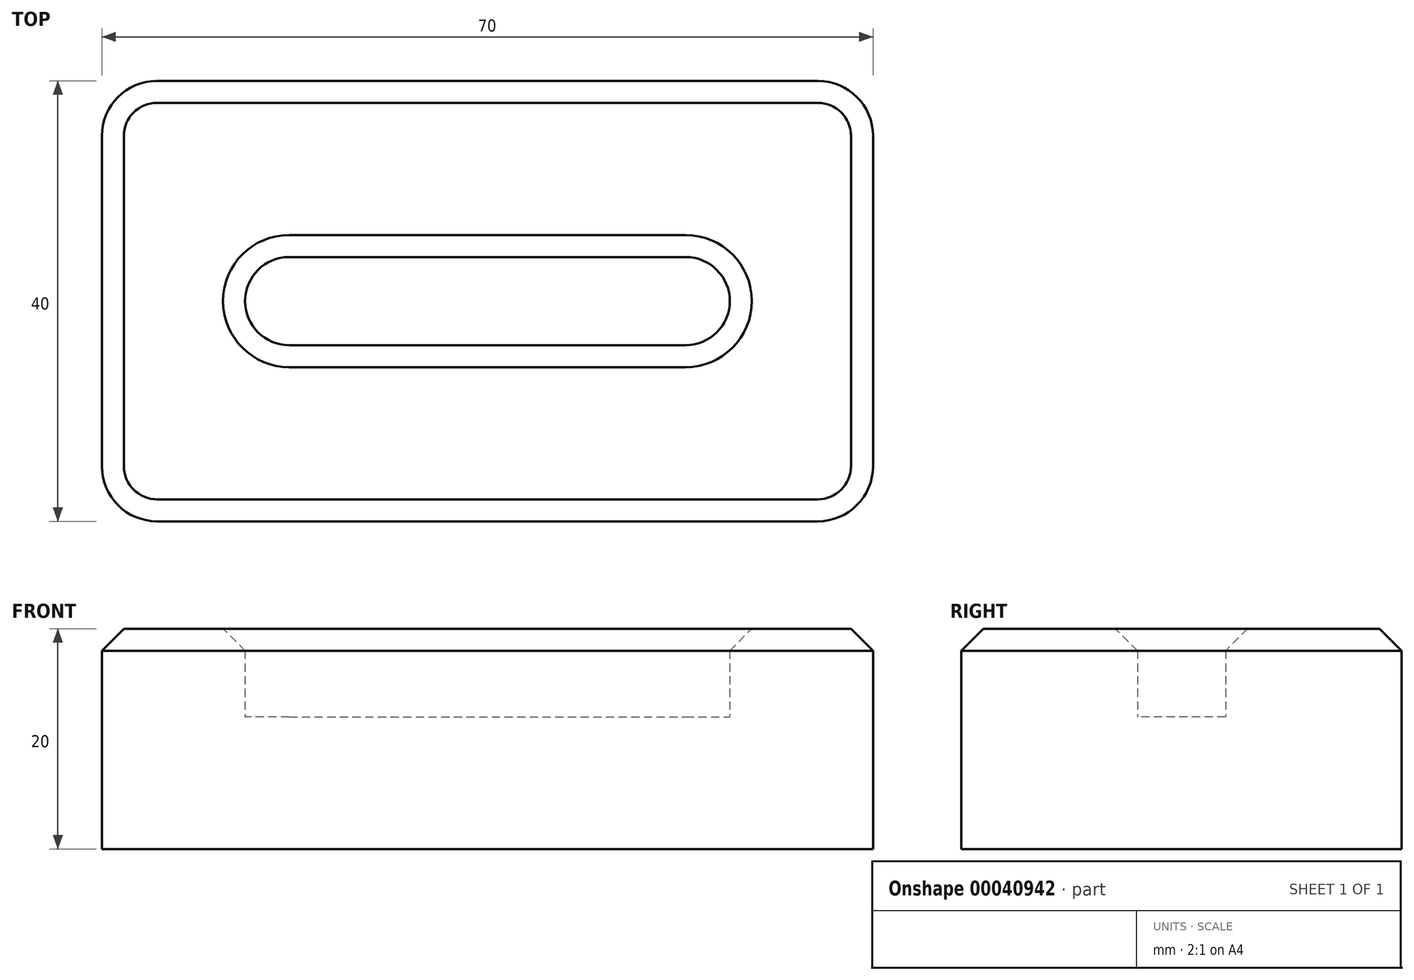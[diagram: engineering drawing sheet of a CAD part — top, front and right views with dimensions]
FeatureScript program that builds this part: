
annotation { "Feature Type Name" : "Feature", "Feature Type Description" : "" }
export const myFeature = defineFeature(function(context is Context, id is Id, definition is map)
    precondition{}
    {
        {
            var Q0;
            Q0=qCreatedBy(makeId("Top.planeOp"),FACE);
            var sketch = newSketch(context, id + "F0", { "sketchPlane" : qUnion([Q0])});
            skLineSegment(sketch, "E0.bottom", {"start": v(-5, 0) * mm, "end": v(-65, 0) * mm});
            skLineSegment(sketch, "E0.top", {"start": v(-5, 40) * mm, "end": v(-65, 40) * mm});
            skLineSegment(sketch, "E0.left", {"start": v(0, 5) * mm, "end": v(0, 35) * mm});
            skLineSegment(sketch, "E0.right", {"start": v(-70, 5) * mm, "end": v(-70, 35) * mm});
            skLineSegment(sketch, "E1.bottom", {"start": v(-53, 24) * mm, "end": v(-17, 24) * mm});
            skLineSegment(sketch, "E1.top", {"start": v(-53, 16) * mm, "end": v(-17, 16) * mm});
            skLineSegment(sketch, "E1.left", {"start": v(-57, 20) * mm, "end": v(-57, 20) * mm});
            skLineSegment(sketch, "E1.right", {"start": v(-13, 20) * mm, "end": v(-13, 20) * mm});
            skPoint(sketch, "E2.visualSharp", {"position": v(-57, 24) * mm});
            skArc(sketch, "E2.filletArc", {"start": v(-53, 24) * mm, "mid": v(-55.83, 22.83) * mm, "end": v(-57, 20) * mm});
            skPoint(sketch, "E3.visualSharp", {"position": v(-57, 16) * mm});
            skArc(sketch, "E3.filletArc", {"start": v(-57, 20) * mm, "mid": v(-55.83, 17.17) * mm, "end": v(-53, 16) * mm});
            skPoint(sketch, "E4.visualSharp", {"position": v(-13, 24) * mm});
            skArc(sketch, "E4.filletArc", {"start": v(-13, 20) * mm, "mid": v(-14.17, 22.83) * mm, "end": v(-17, 24) * mm});
            skPoint(sketch, "E5.visualSharp", {"position": v(-13, 16) * mm});
            skArc(sketch, "E5.filletArc", {"start": v(-17, 16) * mm, "mid": v(-14.17, 17.17) * mm, "end": v(-13, 20) * mm});
            skPoint(sketch, "E6.visualSharp", {"position": v(0, 40) * mm});
            skArc(sketch, "E6.filletArc", {"start": v(0, 35) * mm, "mid": v(-1.46, 38.54) * mm, "end": v(-5, 40) * mm});
            skPoint(sketch, "E7.visualSharp", {"position": v(-70, 40) * mm});
            skArc(sketch, "E7.filletArc", {"start": v(-65, 40) * mm, "mid": v(-68.54, 38.54) * mm, "end": v(-70, 35) * mm});
            skPoint(sketch, "E8.visualSharp", {"position": v(-70, 0) * mm});
            skArc(sketch, "E8.filletArc", {"start": v(-70, 5) * mm, "mid": v(-68.54, 1.46) * mm, "end": v(-65, 0) * mm});
            skPoint(sketch, "E9.visualSharp", {"position": v(0, 0) * mm});
            skArc(sketch, "E9.filletArc", {"start": v(-5, 0) * mm, "mid": v(-1.46, 1.46) * mm, "end": v(0, 5) * mm});
            skSolve(sketch);
        }
        {
            var Q0;
            Q0=makeQuery(id+"F0.imprint","IMPRINT",FACE,{"disambiguationData":[TD([[makeQuery(id+"F0.imprint","IMPRINT",EDGE,{"derivedFrom":sQuery(id+"F0.wireOp",EDGE,"E0.bottom")}),-1.0]])]});
            extrude(context, id + "F1", {"entities" : qUnion([Q0]), "depth" : 20 * mm});
        }
        {
            var Q0;
            Q0=makeQuery(id+"F0.imprint","IMPRINT",FACE,{"disambiguationData":[TD([[makeQuery(id+"F0.imprint","IMPRINT",EDGE,{"derivedFrom":sQuery(id+"F0.wireOp",EDGE,"E1.bottom")}),-1.0]])]});
            extrude(context, id + "F2", {"entities" : qUnion([Q0]), "operationType" : NewBodyOperationType.ADD, "depth" : 12 * mm});
        }
        {
            var Q0;
            Q0=makeQuery(id+"F1.opExtrude","CAP_EDGE",EDGE,{"disambiguationData":[OSD([sQuery(id+"F0.wireOp",EDGE,"E1.bottom")])],"isStart":false});
            var Q1;
            Q1=makeQuery(id+"F1.opExtrude","CAP_EDGE",EDGE,{"disambiguationData":[OSD([sQuery(id+"F0.wireOp",EDGE,"E0.bottom")])],"isStart":false});
            chamfer(context, id + "F3", {"entities" : qUnion([Q0, Q1]), "width" : 2 * mm, "tangentPropagation" : true});
        }
    });
